# Revit family: PRD_AR_CntrTopWshBsns_RondoWashbasin_RNDH451-O,RNDX451-O
name_source: partatom
category: Plumbing Fixtures
revit_build: Autodesk Revit 2018 (Build: 20190510_1515(x64)
units: mm (PartAtom-declared; Revit-internal decimal feet)

## family parameters
Cut with Voids When Loaded = No
Host = Face
OmniClass Number = 23.45.05.14.14
OmniClass Title = Sinks/Lavatories
Part Type = Normal
Room Calculation Point = No
Round Connector Dimension = Use Diameter
Shared = No

## types (2) — shared parameters
AssetType = Fixed
Category = Pr_40_20_96_18, Counter top wash basins
Color = Stainless steel
DrainSize = DN 32 (1 1/4 inch.)
DurationUnit = year
Form = Counter top wash basins
IfcExportAs = IfcSanitaryTerminalType
IfcExportType = WASHHANDBASIN
IntegralAccessories = Lugs for underneath mounting are included
Manufacturer = KWC Group AG
ManufacturerName = KWC Group AG
ManufacturerURL = www.kwc.com
Material = Stainless steel
MaterialsBody = Stainless steel 1.4301
NBSDescription = Counter top wash basins
NBSReference = 45-35-70/360
NominalDepth = 456 mm  [stored 1.49606 ft]
NominalHeight = 159 mm  [stored 0.521654 ft]
NominalWidth = 531 mm  [stored 1.74213 ft]
OutcutDiameterTop = 511 x 436 mm
OutcutDiameterUnderneath = 440 x 320 mm
OverflowKit_E-RNDX-UEL-SET = No
ProductInformation = https://pim.kwc.com
Shape = Oval
Size = 531 x 456 x 159 mm
StandardOverflowKit = Yes
URL = www.kwc.com
Uniclass2015Code = Pr_40_20_96_18
Uniclass2015Title = Counter top wash basins
Uniclass2015Version = Products v1.10
Version = 1
WarrantyDurationUnit = year
WashHandBasinMounting = CounterTop
WashHandBasinType = HandRinse
WasteSize = 32  [stored 0.104987 ft]
WaterSupplyOverflowAndWasteHolesOverflow = Yes
WaterSupplyOverflowAndWasteHolesWaste = Center-Back
WaterSupplyOverflowAndWasteHolesWaterSupply = Single tap hole, middle, 35 mm
zero-valued in all types: Default Elevation

## per-type parameters (varying)
| type | BIMObjectName | Description | Features | Finish | GrossWeight | MaterialsFinishAndColour | Model | ModelNumber | ModelReference | Name | NetWeight | WashbasinMaterial |
| RNDH451-O - High polished | PRD_AR_CounterTopWashBasins_RondoWashbasin_RNDH451-O | Round inset vanity basin, can be mounted from top or underneath, stainless steel, material thickness 1 mm, bowl diameter 450x330 mm, with overflow and tap ledge, incl. 35 mm tap hole drilling, incl. 5/4" overflow kit without waste, stainless steel lugs for underneath mounting are included.

surface high polished
Outcut diameter for mounting from top 511 x 436 mm
Outcut diameter for mounting from underneath 440 x 320 mm | stainless steel, 1.00 mm, high polished, inset mounting, 531x159x456 mm (WxHxD) | High polished | 3.50 kg | High polished | RNDH451-O | 2000056717 | RNDH451-O | RONDO oval inset vanity basin RNDH451-O | 3.50 kg | PRD_AR_StainlessSteel_HighPolished |
| RNDX451-O - Satin finished | PRD_AR_CounterTopWashBasins_RondoWashbasin_RNDX451-O | Round inset vanity basin, can be mounted from top or underneath, stainless steel, material thickness 1 mm, bowl diameter 450x330 mm, with overflow and tap ledge, incl. 35 mm tap hole drilling, incl. 5/4" overflow kit without waste, stainless steel lugs for underneath mounting are included.

surface satin finished
Outcut diameter for mounting from top 511 x 436 mm
Outcut diameter for mounting from underneath 440 x 320 mm | stainless steel, 1.00 mm, satin finished, inset mounting, 531x159x456 mm (WxHxD) | Satin finished | 3.42 kg | Satin finished | RNDX451-O | 2000056719 | RNDX451-O | RONDO oval inset vanity basin RNDX451-O | 3.20 kg | PRD_AR_StainlessSteel_SatinFinished |

note: [stored X ft] marks values corroborated as IEEE doubles in the binary element streams (Revit-internal decimal feet)

## geometry (parser evidence)
native form markers: Sweep x7
no freeform markers — native parametric forms only
